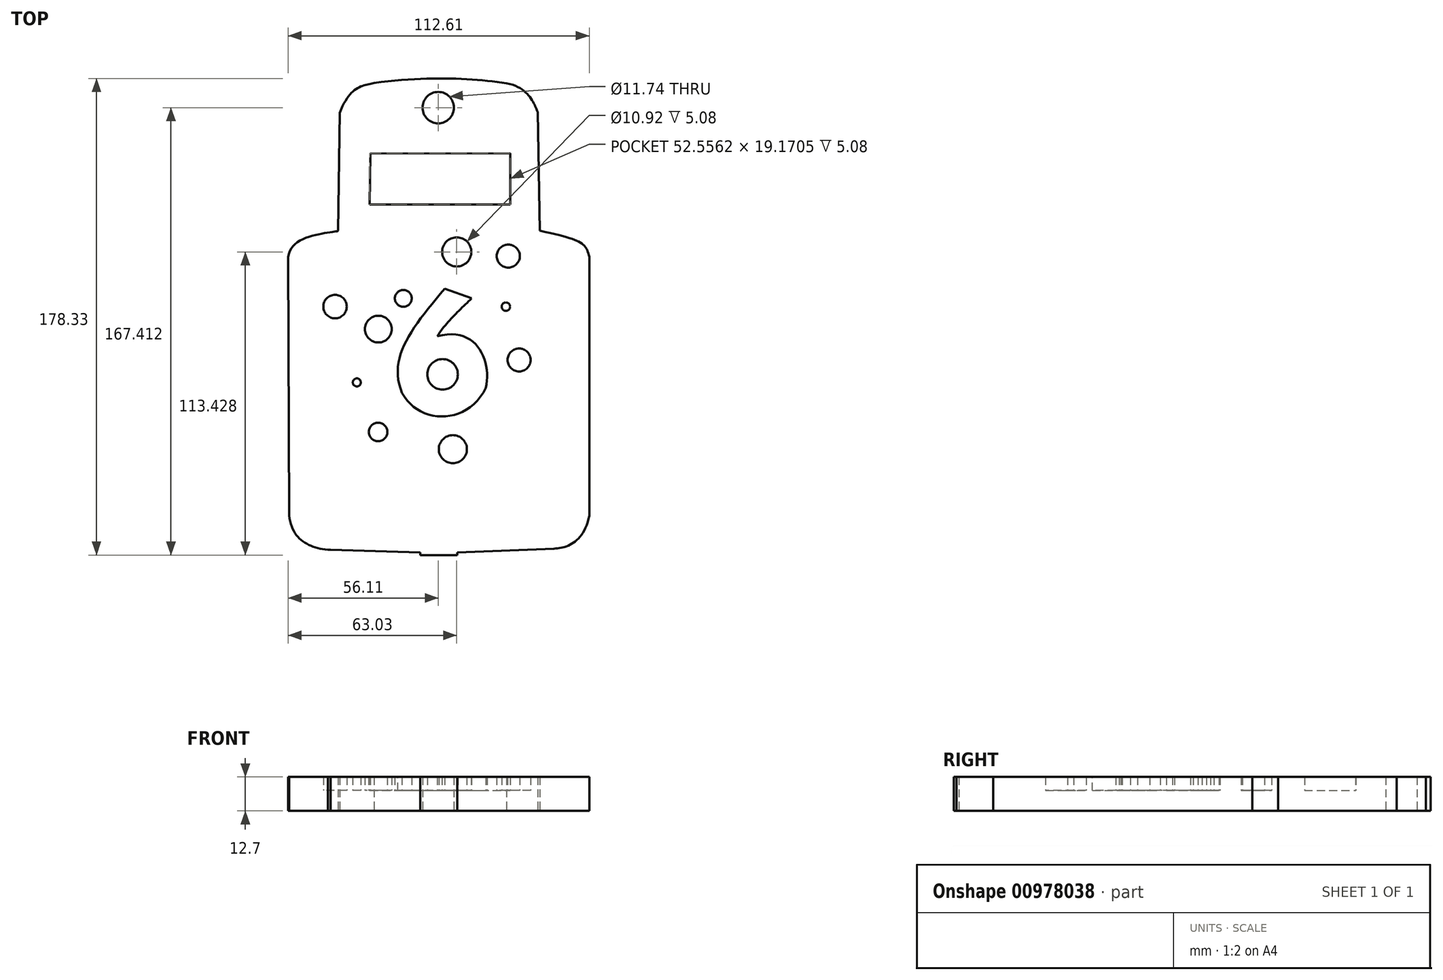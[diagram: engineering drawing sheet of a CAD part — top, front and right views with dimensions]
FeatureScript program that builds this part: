
annotation { "Feature Type Name" : "Feature", "Feature Type Description" : "" }
export const myFeature = defineFeature(function(context is Context, id is Id, definition is map)
    precondition{}
    {
        {
            var Q0;
            Q0=qCreatedBy(makeId("Top.planeOp"),FACE);
            var sketch = newSketch(context, id + "F0", { "sketchPlane" : qUnion([Q0])});
            skLineSegment(sketch, "E0", {"start": v(-121.87, 26.14) * mm, "end": v(-67.2, 26.14) * mm});
            skLineSegment(sketch, "E1", {"start": v(-67.2, 26.14) * mm, "end": v(-67.2, 47.3) * mm});
            skLineSegment(sketch, "E2", {"start": v(-67.2, 47.3) * mm, "end": v(-121.61, 47.3) * mm});
            skLineSegment(sketch, "E3", {"start": v(-121.61, 47.3) * mm, "end": v(-121.87, 26.14) * mm});
            skLineSegment(sketch, "E4", {"start": v(-127.33, 52.76) * mm, "end": v(-61.36, 52.76) * mm});
            skLineSegment(sketch, "E5", {"start": v(-61.36, 52.76) * mm, "end": v(-61.36, 20.68) * mm});
            skLineSegment(sketch, "E6", {"start": v(-61.36, 20.68) * mm, "end": v(-127.2, 20.68) * mm});
            skLineSegment(sketch, "E7", {"start": v(-127.2, 20.68) * mm, "end": v(-127.33, 52.76) * mm});
            skFitSpline(sketch, "E8", {"points": [v(-132.53, 17.42) * mm, v(-151.14, 7.48) * mm], "startDerivative": vector(0, -2.95) * mm, "endDerivative": vector(-2.3, -28.5) * mm});
            skFitSpline(sketch, "E9", {"points": [v(-57.08, 17.36) * mm, v(-38.53, 7.68) * mm], "startDerivative": vector(49.32, -10.6) * mm, "endDerivative": vector(4.4, -15.43) * mm});
            skLineSegment(sketch, "E10", {"start": v(-151.14, 7.48) * mm, "end": v(-150.8, -89.19) * mm});
            skLineSegment(sketch, "E11", {"start": v(-38.53, 7.68) * mm, "end": v(-38.53, -89.23) * mm});
            skFitSpline(sketch, "E12", {"points": [v(-150.8, -89.19) * mm, v(-136.36, -101.97) * mm], "startDerivative": vector(3.21, -26.38) * mm, "endDerivative": vector(22.47, -2.32) * mm});
            skFitSpline(sketch, "E13", {"points": [v(-38.53, -89.23) * mm, v(-51.76, -101.54) * mm], "startDerivative": vector(-6.43, -30.37) * mm, "endDerivative": vector(-14.74, -0.52) * mm});
            skLineSegment(sketch, "E14", {"start": v(-136.36, -101.97) * mm, "end": v(-135.28, -101.97) * mm});
            skLineSegment(sketch, "E15", {"start": v(-135.28, -101.97) * mm, "end": v(-101.68, -103.05) * mm});
            skLineSegment(sketch, "E16", {"start": v(-51.76, -101.54) * mm, "end": v(-87.86, -102.98) * mm});
            skLineSegment(sketch, "E17", {"start": v(-101.68, -103.05) * mm, "end": v(-101.71, -104) * mm});
            skLineSegment(sketch, "E18", {"start": v(-101.71, -104) * mm, "end": v(-87.85, -104) * mm});
            skLineSegment(sketch, "E19", {"start": v(-87.85, -104) * mm, "end": v(-87.86, -102.98) * mm});
            skLineSegment(sketch, "E20", {"start": v(-132.53, 17.42) * mm, "end": v(-131.8, 61.53) * mm});
            skLineSegment(sketch, "E21", {"start": v(-57.08, 17.36) * mm, "end": v(-57.76, 61.68) * mm});
            skFitSpline(sketch, "E22", {"points": [v(-131.8, 61.53) * mm, v(-119.06, 72.69) * mm], "startDerivative": vector(11.1, 30.56) * mm, "endDerivative": vector(11.34, 2.98) * mm});
            skFitSpline(sketch, "E23", {"points": [v(-57.76, 61.68) * mm, v(-69.45, 72.55) * mm], "startDerivative": vector(-3, 5.35) * mm, "endDerivative": vector(-27.68, 5.44) * mm});
            skFitSpline(sketch, "E24", {"points": [v(-119.06, 72.69) * mm, v(-69.45, 72.55) * mm], "startDerivative": vector(61.59, 7.7) * mm, "endDerivative": vector(40.06, -5.98) * mm});
            skCircle(sketch, "E25", {"center": v(-93.4, -36.36) * mm, "radius": 5.72 * mm});
            skCircle(sketch, "E26", {"center": v(-93.4, -36.36) * mm, "radius": 7.2 * mm});
            skLineSegment(sketch, "E27", {"start": v(-92.56, -2.72) * mm, "end": v(-79.02, -7.56) * mm});
            skFitSpline(sketch, "E28", {"points": [v(-92.56, -2.72) * mm, v(-108.08, -47.03) * mm], "startDerivative": vector(-22.1, -25.48) * mm, "endDerivative": vector(38.23, -48.19) * mm});
            skFitSpline(sketch, "E29", {"points": [v(-79.02, -7.56) * mm, v(-91.71, -19.8) * mm], "startDerivative": vector(-13.8, -10.4) * mm, "endDerivative": vector(-10.8, -13.28) * mm});
            skFitSpline(sketch, "E30", {"points": [v(-91.71, -19.8) * mm, v(-78.18, -46.75) * mm], "startDerivative": vector(59.7, 1.44) * mm, "endDerivative": vector(-14.69, -11.26) * mm});
            skFitSpline(sketch, "E31", {"points": [v(-108.08, -47.03) * mm, v(-78.18, -46.75) * mm], "startDerivative": vector(23.84, -29.26) * mm, "endDerivative": vector(14.44, 24.73) * mm});
            skLineSegment(sketch, "E32", {"start": v(-120.71, 27.23) * mm, "end": v(-68.16, 27.23) * mm});
            skLineSegment(sketch, "E33", {"start": v(-68.16, 27.23) * mm, "end": v(-68.16, 46.4) * mm});
            skLineSegment(sketch, "E34", {"start": v(-120.71, 27.23) * mm, "end": v(-120.48, 46.26) * mm});
            skLineSegment(sketch, "E35", {"start": v(-120.48, 46.26) * mm, "end": v(-68.16, 46.4) * mm});
            skLineSegment(sketch, "E36", {"start": v(-92.56, -4.34) * mm, "end": v(-82.5, -7.92) * mm});
            skFitSpline(sketch, "E37", {"points": [v(-92.56, -4.34) * mm, v(-108.56, -43.36) * mm], "startDerivative": vector(-38.58, -45.3) * mm, "endDerivative": vector(16.14, -38.88) * mm});
            skFitSpline(sketch, "E38", {"points": [v(-82.5, -7.92) * mm, v(-95.4, -22.15) * mm], "startDerivative": vector(-13.54, -13.18) * mm, "endDerivative": vector(-10.53, -16.72) * mm});
            skFitSpline(sketch, "E39", {"points": [v(-95.4, -22.15) * mm, v(-77.2, -41.4) * mm], "startDerivative": vector(45.4, 12.52) * mm, "endDerivative": vector(-6.09, -29.43) * mm});
            skFitSpline(sketch, "E40", {"points": [v(-108.56, -43.36) * mm, v(-77.2, -41.4) * mm], "startDerivative": vector(19.3, -35.5) * mm, "endDerivative": vector(20.69, 42.43) * mm});
            skCircle(sketch, "E41", {"center": v(-133.61, -11.01) * mm, "radius": 4.39 * mm});
            skCircle(sketch, "E42", {"center": v(-125.48, -39.38) * mm, "radius": 1.5 * mm});
            skCircle(sketch, "E43", {"center": v(-108.08, -7.92) * mm, "radius": 3.15 * mm});
            skCircle(sketch, "E44", {"center": v(-69.72, -11.02) * mm, "radius": 1.57 * mm});
            skCircle(sketch, "E45", {"center": v(-64.77, -30.96) * mm, "radius": 4.3 * mm});
            skCircle(sketch, "E46", {"center": v(-117.51, -57.92) * mm, "radius": 3.48 * mm});
            skCircle(sketch, "E47", {"center": v(-89.56, -64.37) * mm, "radius": 5.26 * mm});
            skCircle(sketch, "E48", {"center": v(-117.42, -19.44) * mm, "radius": 5 * mm});
            skCircle(sketch, "E49", {"center": v(-68.83, 7.9) * mm, "radius": 4.32 * mm});
            skCircle(sketch, "E50", {"center": v(-88.1, 9.44) * mm, "radius": 5.46 * mm});
            skCircle(sketch, "E51", {"center": v(-95.03, 63.42) * mm, "radius": 5.87 * mm});
            skSolve(sketch);
        }
        {
            var Q0;
            Q0=makeQuery(id+"F0.imprint","IMPRINT",FACE,{"disambiguationData":[TD([[makeQuery(id+"F0.imprint","IMPRINT",EDGE,{"derivedFrom":sQuery(id+"F0.wireOp",EDGE,"E4")}),1.0]])]});
            var Q1;
            Q1=makeQuery(id+"F0.imprint","IMPRINT",FACE,{"disambiguationData":[TD([[makeQuery(id+"F0.imprint","IMPRINT",EDGE,{"derivedFrom":sQuery(id+"F0.wireOp",EDGE,"E27")}),-1.0]])]});
            var Q2;
            Q2=makeQuery(id+"F0.imprint","IMPRINT",FACE,{"disambiguationData":[TD([[makeQuery(id+"F0.imprint","IMPRINT",EDGE,{"derivedFrom":sQuery(id+"F0.wireOp",EDGE,"E0")}),-1.0]])]});
            var Q3;
            Q3=makeQuery(id+"F0.imprint","IMPRINT",FACE,{"disambiguationData":[TD([[makeQuery(id+"F0.imprint","IMPRINT",EDGE,{"derivedFrom":sQuery(id+"F0.wireOp",EDGE,"E0")}),1.0]])]});
            extrude(context, id + "F1", {"entities" : qUnion([Q0, Q1, Q2, Q3]), "depth" : 12.7 * mm, "offsetDistance" : 25.4 * mm});
        }
        {
            var Q0;
            Q0=makeQuery(id+"F0.imprint","IMPRINT",FACE,{"disambiguationData":[TD([[makeQuery(id+"F0.imprint","IMPRINT",EDGE,{"derivedFrom":sQuery(id+"F0.wireOp",EDGE,"E50")}),1.0]])]});
            var Q1;
            Q1=makeQuery(id+"F0.imprint","IMPRINT",FACE,{"disambiguationData":[TD([[makeQuery(id+"F0.imprint","IMPRINT",EDGE,{"derivedFrom":sQuery(id+"F0.wireOp",EDGE,"E49")}),1.0]])]});
            var Q2;
            Q2=makeQuery(id+"F0.imprint","IMPRINT",FACE,{"disambiguationData":[TD([[makeQuery(id+"F0.imprint","IMPRINT",EDGE,{"derivedFrom":sQuery(id+"F0.wireOp",EDGE,"E44")}),1.0]])]});
            var Q3;
            Q3=makeQuery(id+"F0.imprint","IMPRINT",FACE,{"disambiguationData":[TD([[makeQuery(id+"F0.imprint","IMPRINT",EDGE,{"derivedFrom":sQuery(id+"F0.wireOp",EDGE,"E45")}),1.0]])]});
            var Q4;
            Q4=makeQuery(id+"F0.imprint","IMPRINT",FACE,{"disambiguationData":[TD([[makeQuery(id+"F0.imprint","IMPRINT",EDGE,{"derivedFrom":sQuery(id+"F0.wireOp",EDGE,"E43")}),1.0]])]});
            var Q5;
            Q5=makeQuery(id+"F0.imprint","IMPRINT",FACE,{"disambiguationData":[TD([[makeQuery(id+"F0.imprint","IMPRINT",EDGE,{"derivedFrom":sQuery(id+"F0.wireOp",EDGE,"E48")}),1.0]])]});
            var Q6;
            Q6=makeQuery(id+"F0.imprint","IMPRINT",FACE,{"disambiguationData":[TD([[makeQuery(id+"F0.imprint","IMPRINT",EDGE,{"derivedFrom":sQuery(id+"F0.wireOp",EDGE,"E41")}),1.0]])]});
            var Q7;
            Q7=makeQuery(id+"F0.imprint","IMPRINT",FACE,{"disambiguationData":[TD([[makeQuery(id+"F0.imprint","IMPRINT",EDGE,{"derivedFrom":sQuery(id+"F0.wireOp",EDGE,"E42")}),1.0]])]});
            var Q8;
            Q8=makeQuery(id+"F0.imprint","IMPRINT",FACE,{"disambiguationData":[TD([[makeQuery(id+"F0.imprint","IMPRINT",EDGE,{"derivedFrom":sQuery(id+"F0.wireOp",EDGE,"E46")}),1.0]])]});
            var Q9;
            Q9=makeQuery(id+"F0.imprint","IMPRINT",FACE,{"disambiguationData":[TD([[makeQuery(id+"F0.imprint","IMPRINT",EDGE,{"derivedFrom":sQuery(id+"F0.wireOp",EDGE,"E47")}),1.0]])]});
            var Q10;
            Q10=makeQuery(id+"F0.imprint","IMPRINT",FACE,{"disambiguationData":[TD([[makeQuery(id+"F0.imprint","IMPRINT",EDGE,{"derivedFrom":sQuery(id+"F0.wireOp",EDGE,"E26")}),-1.0]])]});
            var Q11;
            Q11=makeQuery(id+"F0.imprint","IMPRINT",FACE,{"disambiguationData":[TD([[makeQuery(id+"F0.imprint","IMPRINT",EDGE,{"derivedFrom":sQuery(id+"F0.wireOp",EDGE,"E32")}),1.0]])]});
            var Q12;
            Q12=makeQuery(id+"F0.imprint","IMPRINT",FACE,{"disambiguationData":[TD([[makeQuery(id+"F0.imprint","IMPRINT",EDGE,{"derivedFrom":sQuery(id+"F0.wireOp",EDGE,"E25")}),1.0]])]});
            var Q13;
            Q13=makeQuery(id+"F0.imprint","IMPRINT",FACE,{"disambiguationData":[TD([[makeQuery(id+"F0.imprint","IMPRINT",EDGE,{"derivedFrom":sQuery(id+"F0.wireOp",EDGE,"E25")}),-1.0]])]});
            extrude(context, id + "F2", {"entities" : qUnion([Q0, Q1, Q2, Q3, Q4, Q5, Q6, Q7, Q8, Q9, Q10, Q11, Q12, Q13]), "operationType" : NewBodyOperationType.ADD, "depth" : 7.62 * mm, "offsetDistance" : 25.4 * mm});
        }
        {
            var Q0;
            Q0=makeQuery(id+"F0.imprint","IMPRINT",FACE,{"disambiguationData":[TD([[makeQuery(id+"F0.imprint","IMPRINT",EDGE,{"derivedFrom":sQuery(id+"F0.wireOp",EDGE,"E25")}),1.0]])]});
            extrude(context, id + "F3", {"entities" : qUnion([Q0]), "operationType" : NewBodyOperationType.ADD, "depth" : 12.7 * mm, "offsetDistance" : 25.4 * mm});
        }
    });
